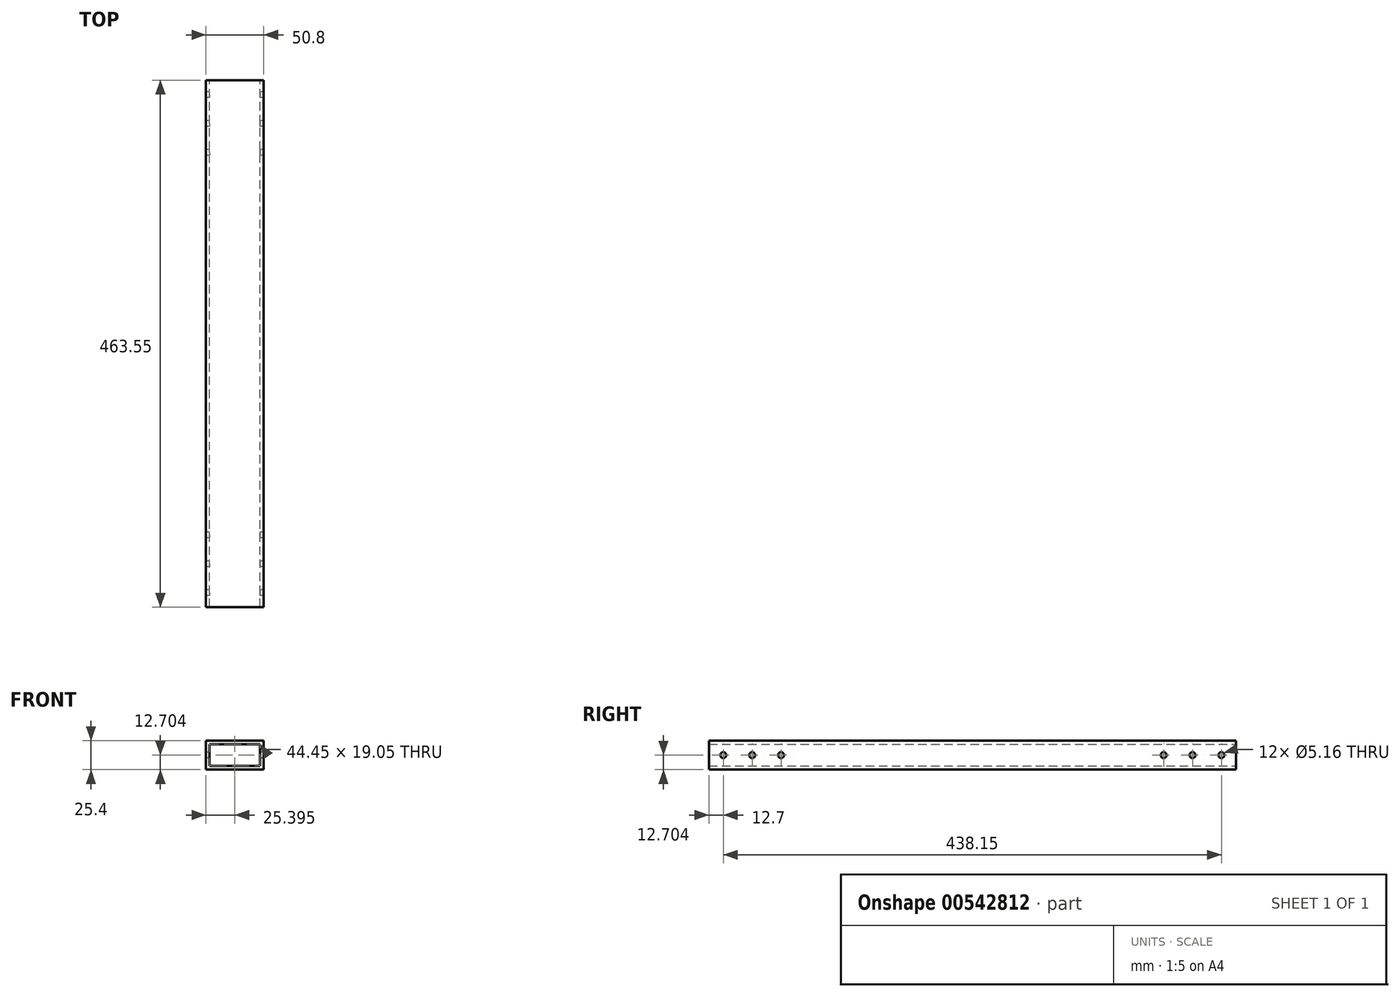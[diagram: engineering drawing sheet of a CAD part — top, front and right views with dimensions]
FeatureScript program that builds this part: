
annotation { "Feature Type Name" : "Feature", "Feature Type Description" : "" }
export const myFeature = defineFeature(function(context is Context, id is Id, definition is map)
    precondition{}
    {
        {
            var Q0;
            Q0=qCreatedBy(makeId("Front.planeOp"),FACE);
            var sketch = newSketch(context, id + "F0", { "sketchPlane" : qUnion([Q0])});
            skLineSegment(sketch, "E0.bottom", {"start": v(-31.97, 16.3) * mm, "end": v(18.83, 16.3) * mm});
            skLineSegment(sketch, "E0.top", {"start": v(-31.97, -9.1) * mm, "end": v(18.83, -9.1) * mm});
            skLineSegment(sketch, "E0.left", {"start": v(-31.97, 16.3) * mm, "end": v(-31.97, -9.1) * mm});
            skLineSegment(sketch, "E0.right", {"start": v(18.83, 16.3) * mm, "end": v(18.83, -9.1) * mm});
            skLineSegment(sketch, "E1.bottom", {"start": v(-28.8, 13.12) * mm, "end": v(15.65, 13.12) * mm});
            skLineSegment(sketch, "E1.top", {"start": v(-28.8, -5.93) * mm, "end": v(15.65, -5.93) * mm});
            skLineSegment(sketch, "E1.left", {"start": v(-28.8, 13.12) * mm, "end": v(-28.8, -5.93) * mm});
            skLineSegment(sketch, "E1.right", {"start": v(15.65, 13.12) * mm, "end": v(15.65, -5.93) * mm});
            skSolve(sketch);
        }
        {
            var Q0;
            Q0=makeQuery(id+"F0.imprint","IMPRINT",FACE,{"disambiguationData":[TD([[makeQuery(id+"F0.imprint","IMPRINT",EDGE,{"derivedFrom":sQuery(id+"F0.wireOp",EDGE,"E0.bottom")}),-1.0]])]});
            extrude(context, id + "F1", {"entities" : qUnion([Q0]), "depth" : 463.55 * mm});
        }
        {
            var Q0;
            Q0=makeQuery(id+"F1.opExtrude","SWEPT_FACE",FACE,{"disambiguationData":[OSD([sQuery(id+"F0.wireOp",EDGE,"E0.left")])]});
            var sketch = newSketch(context, id + "F2", { "sketchPlane" : qUnion([Q0])});
            skCircle(sketch, "E2", {"center": v(450.85, 3.6) * mm, "radius": 2.58 * mm});
            skPoint(sketch, "E2.centerSnap0", {"position": v(463.55, 3.6) * mm});
            skCircle(sketch, "E3", {"center": v(425.45, 3.6) * mm, "radius": 2.58 * mm});
            skCircle(sketch, "E4", {"center": v(400.05, 3.6) * mm, "radius": 2.58 * mm});
            skCircle(sketch, "E5", {"center": v(12.7, 3.6) * mm, "radius": 2.58 * mm});
            skPoint(sketch, "E5.centerSnap0", {"position": v(0, 3.6) * mm});
            skCircle(sketch, "E6", {"center": v(38.1, 3.6) * mm, "radius": 2.58 * mm});
            skCircle(sketch, "E7", {"center": v(63.5, 3.6) * mm, "radius": 2.58 * mm});
            skSolve(sketch);
        }
        {
            var Q0;
            Q0=makeQuery(id+"F2.imprint","IMPRINT",FACE,{"disambiguationData":[TD([[makeQuery(id+"F2.imprint","IMPRINT",EDGE,{"derivedFrom":sQuery(id+"F2.wireOp",EDGE,"E5")}),1.0]])]});
            var Q1;
            Q1=makeQuery(id+"F2.imprint","IMPRINT",FACE,{"disambiguationData":[TD([[makeQuery(id+"F2.imprint","IMPRINT",EDGE,{"derivedFrom":sQuery(id+"F2.wireOp",EDGE,"E6")}),1.0]])]});
            var Q2;
            Q2=makeQuery(id+"F2.imprint","IMPRINT",FACE,{"disambiguationData":[TD([[makeQuery(id+"F2.imprint","IMPRINT",EDGE,{"derivedFrom":sQuery(id+"F2.wireOp",EDGE,"E7")}),1.0]])]});
            var Q3;
            Q3=makeQuery(id+"F2.imprint","IMPRINT",FACE,{"disambiguationData":[TD([[makeQuery(id+"F2.imprint","IMPRINT",EDGE,{"derivedFrom":sQuery(id+"F2.wireOp",EDGE,"E4")}),1.0]])]});
            var Q4;
            Q4=makeQuery(id+"F2.imprint","IMPRINT",FACE,{"disambiguationData":[TD([[makeQuery(id+"F2.imprint","IMPRINT",EDGE,{"derivedFrom":sQuery(id+"F2.wireOp",EDGE,"E3")}),1.0]])]});
            var Q5;
            Q5=makeQuery(id+"F2.imprint","IMPRINT",FACE,{"disambiguationData":[TD([[makeQuery(id+"F2.imprint","IMPRINT",EDGE,{"derivedFrom":sQuery(id+"F2.wireOp",EDGE,"E2")}),1.0]])]});
            extrude(context, id + "F3", {"entities" : qUnion([Q0, Q1, Q2, Q3, Q4, Q5]), "operationType" : NewBodyOperationType.REMOVE, "endBound" : BoundingType.THROUGH_ALL, "oppositeDirection" : true, "depth" : 25.4 * mm, "offsetDistance" : 25.4 * mm});
        }
    });
